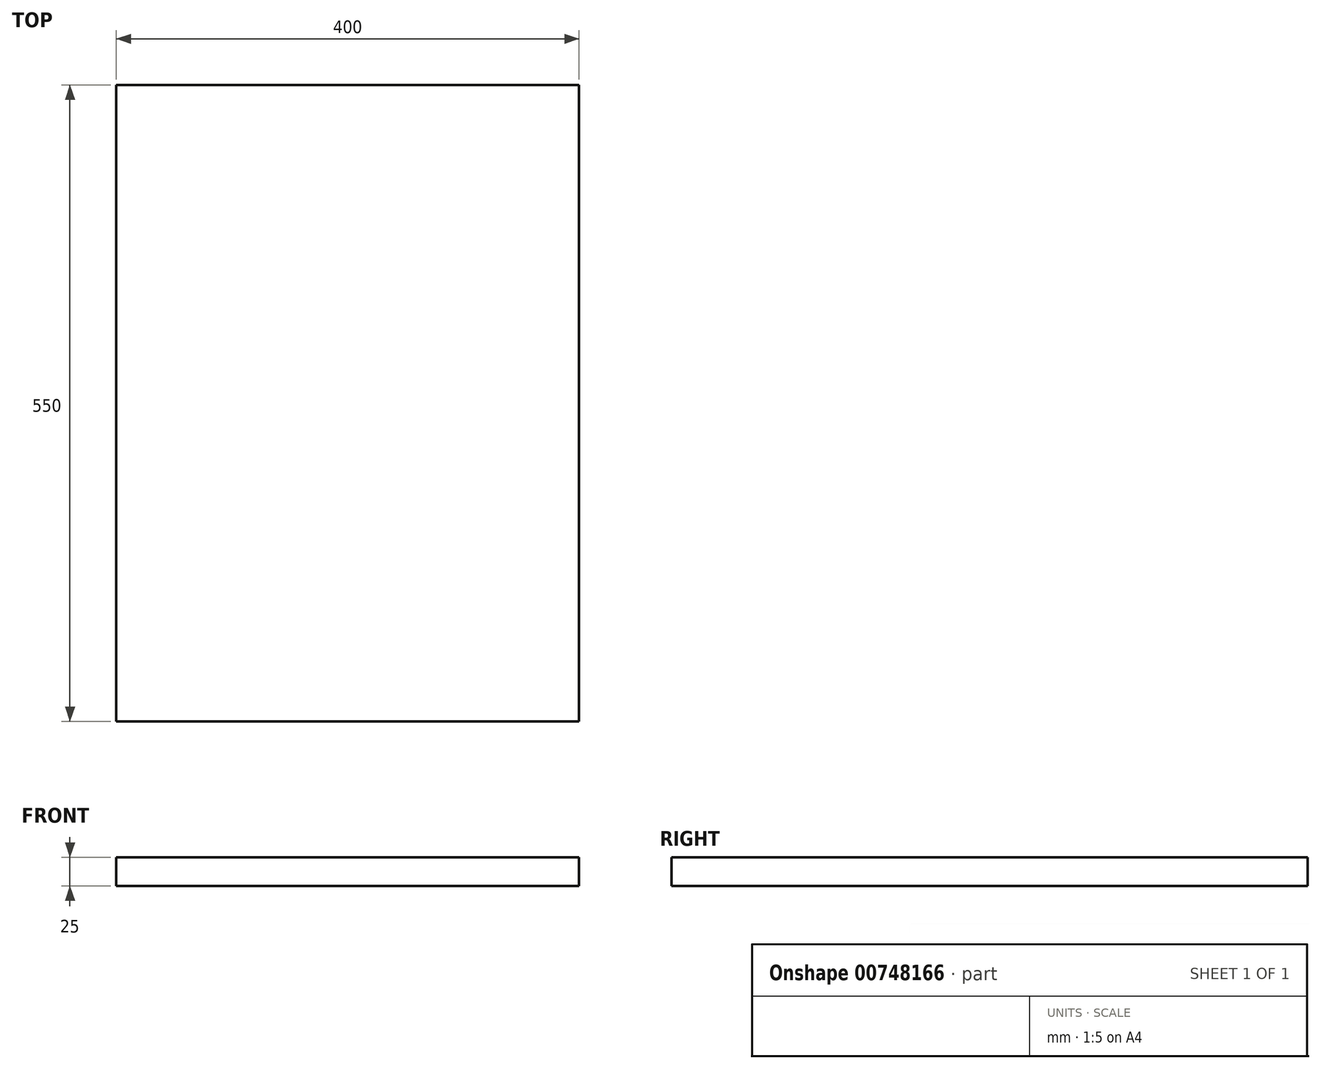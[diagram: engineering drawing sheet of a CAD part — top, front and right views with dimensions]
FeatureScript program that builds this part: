
annotation { "Feature Type Name" : "Feature", "Feature Type Description" : "" }
export const myFeature = defineFeature(function(context is Context, id is Id, definition is map)
    precondition{}
    {
        {
            var Q0;
            Q0=qCreatedBy(makeId("Front.planeOp"),FACE);
            var sketch = newSketch(context, id + "F0", { "sketchPlane" : qUnion([Q0])});
            skLineSegment(sketch, "E0.bottom", {"start": v(0, 0) * mm, "end": v(-400, 0) * mm});
            skLineSegment(sketch, "E0.top", {"start": v(0, 25) * mm, "end": v(-400, 25) * mm});
            skLineSegment(sketch, "E0.left", {"start": v(0, 0) * mm, "end": v(0, 25) * mm});
            skLineSegment(sketch, "E0.right", {"start": v(-400, 0) * mm, "end": v(-400, 25) * mm});
            skSolve(sketch);
        }
        {
            var Q0;
            Q0 = qSketchRegion(id + "F0", true);
            extrude(context, id + "F1", {"entities" : qUnion([Q0]), "depth" : 550 * mm, "offsetDistance" : 25 * mm});
        }
    });
